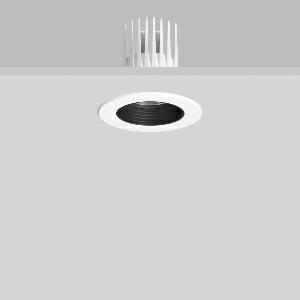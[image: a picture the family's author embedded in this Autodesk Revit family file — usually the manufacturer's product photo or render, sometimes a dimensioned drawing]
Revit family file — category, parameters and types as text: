
# Revit family: heledon_mini_e_901746_002_1_a302
name_source: partatom
category: Lighting Fixtures
units: mm (PartAtom-declared; Revit-internal decimal feet)

## family parameters
Cut with Voids When Loaded = No
Host = Face
Light Source = No
Part Type = Normal
Room Calculation Point = No
Round Connector Dimension = Use Diameter
Shared = No

## types (1)
- HELEDON mini E (1 x LED Modul 940, 2450 lm, 4000)
    Apparent Load = 20 VA
    Approval mark = CE
    CIE Flux Codes = 80 99 100 100 100
    Color Rendering = 92
    Color Temperature = 4000
    Default Elevation = 1800 mm
    Description = Series: HELEDON mini
Round recessed downlight. Housing: die-cast aluminium, powder-coated. Black plastic ring and recessed LED to prevent glare from the side. Optical assembly with lens made of plastic (polycarbonate) for the best homogeneous light distribution - can be changed without tools. Best colour rendering index Ra>90. Suitable for Recessed ceiling mounting. Installation without tools thanks to spring fastening system. Including separate LED converter with connecting cable 600 mm.High quality converter without flickering and stroboscopic effect. Through-wiring box (5 pole) available as accessory. The following accessories can be mounted without use of tools: interchangeable lenses, decorative glasses, honeycomb louvre, clear and frosted diffusers, white interchangeable plastic ring. 
Colour: traffic white, matt (RAL 9016)
Diameter: 124 mm
Height: 3 mm
Cut-out diameter: 114 mm
Recess height: 170 mm
Luminaire: recess height: 120 mm
Lamp: LED
Socket: without socket
Colour temperature: 4000K
Colour rendering index (CRI): 92
System power: 20 W
Rated luminous flux: 2450 lm
Luminous efficiency: 123 lm/W
Control gear: Regulated power supply
Protection class: II
Type of protection: IP 20
    Height = 0 mm  [stored 0 ft]
    Lamp = 1 x LED Modul 940
    Lamp Light Flux = 2450 lm
    Lamp count = 1
    Length = 124 mm  [stored 0.406824 ft]
    Lifetime = 50000 h
    Luminous efficacy = 123 lm/W
    Manufacturer = RZB
    ModVariant = No
    Model = 901746.002.1
    Mounting Place = Ceiling
    Mounting Type = Recessed
    Number of Poles = 1
    OnlyDefault = Yes
    Power Factor = 1
    Product Name = HELEDON mini E
    Product group = Recessed downlights
    ProductGroupID = 402
    Protection Class = Protection class II
    Protection Degree = IP 20
    RLX_Detail_Level = 1
    RLX_Emergency_Light_Flux = 0 lm
    RLX_Emergency_Type = 0
    RLX_Emergency_Type_DB = No
    RlxData = <blob elided: 123249 chars, md5=ec01ee0f>
    Socket = socket
    Standby Power = 0 W
    System Light Flux = 2450 lm
    System Power = 20 W
    Type Comments = Product without accessories
    Type Image = 901656.002.jpg
    URL = http://relux.com
    VarID = ---
    Voltage = 230 V
    Voltage Range = 220-240 V
    Weight = 0.00 kg
    Width = 0 mm  [stored 0 ft]

note: [stored X ft] marks values corroborated as IEEE doubles in the binary element streams (Revit-internal decimal feet)

## geometry (parser evidence)
native form markers: Blend x4, Sweep x13
no freeform markers — native parametric forms only
